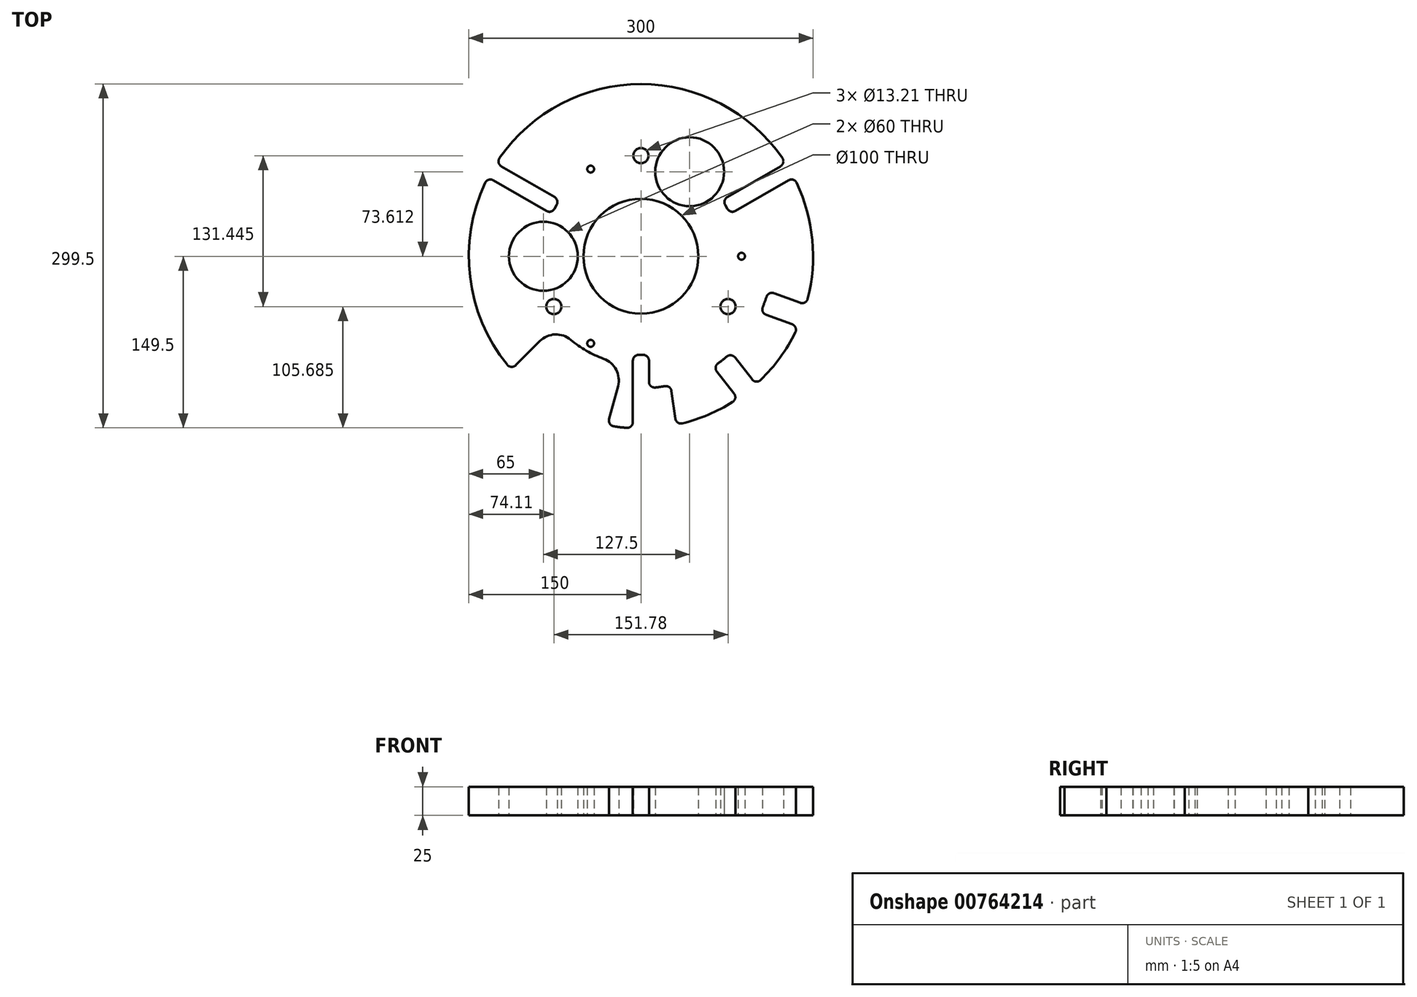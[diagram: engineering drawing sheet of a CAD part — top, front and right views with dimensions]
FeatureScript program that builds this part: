
annotation { "Feature Type Name" : "Feature", "Feature Type Description" : "" }
export const myFeature = defineFeature(function(context is Context, id is Id, definition is map)
    precondition{}
    {
        {
            var Q0;
            Q0=qCreatedBy(makeId("Top.planeOp"),FACE);
            var sketch = newSketch(context, id + "F0", { "sketchPlane" : qUnion([Q0])});
            skLineSegment(sketch, "E0.bottom", {"start": v(-7.02, -85.93) * mm, "end": v(7.03, -85.93) * mm});
            skLineSegment(sketch, "E0.left", {"start": v(-7.02, -85.93) * mm, "end": v(-7.02, -149.84) * mm});
            skLineSegment(sketch, "E0.right", {"start": v(7.03, -85.93) * mm, "end": v(7.03, -114.79) * mm});
            skLineSegment(sketch, "E1", {"start": v(0, 0) * mm, "end": v(20.33, -144.63) * mm, "construction": true});
            skCircle(sketch, "E2", {"center": v(0, 87.63) * mm, "radius": 6.6 * mm});
            skCircle(sketch, "E3.1.0", {"center": v(-75.89, -43.81) * mm, "radius": 6.6 * mm});
            skCircle(sketch, "E3.2.0", {"center": v(75.89, -43.82) * mm, "radius": 6.6 * mm});
            skPoint(sketch, "E3.center", {"position": v(0, 0) * mm});
            skLineSegment(sketch, "E4.1.0", {"start": v(77.93, 36.88) * mm, "end": v(133.27, 68.83) * mm});
            skLineSegment(sketch, "E4.1.1", {"start": v(77.93, 36.88) * mm, "end": v(70.9, 49.05) * mm});
            skLineSegment(sketch, "E4.1.2", {"start": v(70.9, 49.05) * mm, "end": v(126.25, 81) * mm});
            skLineSegment(sketch, "E4.2.0", {"start": v(-70.9, 49.05) * mm, "end": v(-126.25, 81) * mm});
            skLineSegment(sketch, "E4.2.1", {"start": v(-70.9, 49.05) * mm, "end": v(-77.93, 36.88) * mm});
            skLineSegment(sketch, "E4.2.2", {"start": v(-77.93, 36.88) * mm, "end": v(-133.27, 68.83) * mm});
            skArc(sketch, "E5.trimOffspring", {"start": v(-133.27, 68.83) * mm, "mid": v(-148.9, -18.1) * mm, "end": v(-112.9, -98.76) * mm});
            skCircle(sketch, "E6", {"center": v(0, 0) * mm, "radius": 50 * mm});
            skLineSegment(sketch, "E7", {"start": v(0, 0) * mm, "end": v(-98.81, -98.81) * mm, "construction": true});
            skLineSegment(sketch, "E8", {"start": v(0, 0) * mm, "end": v(85.73, -109.22) * mm, "construction": true});
            skLineSegment(sketch, "E9", {"start": v(0, 0) * mm, "end": v(123.83, -45.72) * mm, "construction": true});
            skLineSegment(sketch, "E10.trimOffspring", {"start": v(110.94, -30.3) * mm, "end": v(144.18, -42.57) * mm});
            skLineSegment(sketch, "E11.trimOffspring", {"start": v(104, -49.06) * mm, "end": v(137.25, -61.34) * mm});
            skLineSegment(sketch, "E12.trimOffspring", {"start": v(78.6, -83.94) * mm, "end": v(100.48, -111.82) * mm});
            skLineSegment(sketch, "E13.trimOffspring", {"start": v(62.87, -96.3) * mm, "end": v(84.75, -124.17) * mm});
            skLineSegment(sketch, "E14.trimOffspring", {"start": v(25.85, -112.06) * mm, "end": v(30.73, -146.82) * mm});
            skLineSegment(sketch, "E15.trimOffspring", {"start": v(-98.76, -112.9) * mm, "end": v(-99, -113.14) * mm});
            skLineSegment(sketch, "E16.trimOffspring", {"start": v(-73.87, -59.73) * mm, "end": v(-113.14, -99) * mm});
            skArc(sketch, "E17.trimOffspring", {"start": v(7.03, -114.79) * mm, "mid": v(16.5, -113.81) * mm, "end": v(25.85, -112.06) * mm});
            skArc(sketch, "E18.trimOffspring", {"start": v(62.87, -96.3) * mm, "mid": v(71, -90.46) * mm, "end": v(78.6, -83.94) * mm});
            skArc(sketch, "E19.trimOffspring", {"start": v(104, -49.06) * mm, "mid": v(107.88, -39.83) * mm, "end": v(110.94, -30.3) * mm});
            skArc(sketch, "E20.trimOffspring", {"start": v(30.73, -146.82) * mm, "mid": v(58.77, -138) * mm, "end": v(84.54, -123.9) * mm});
            skPoint(sketch, "E21.start.orphan", {"position": v(7.03, -149.84) * mm});
            skPoint(sketch, "E22.center.orphan", {"position": v(20.33, -144.63) * mm});
            skArc(sketch, "E23.trimOffspring", {"start": v(100.28, -111.56) * mm, "mid": v(121.25, -88.31) * mm, "end": v(136.94, -61.22) * mm});
            skPoint(sketch, "E24.center.orphan", {"position": v(85.73, -109.22) * mm});
            skArc(sketch, "E25.trimOffspring", {"start": v(143.87, -42.46) * mm, "mid": v(149.33, 14.21) * mm, "end": v(133.27, 68.83) * mm});
            skPoint(sketch, "E26.center.orphan", {"position": v(123.83, -45.72) * mm});
            skArc(sketch, "E27.trimOffspring", {"start": v(-29.08, -147.15) * mm, "mid": v(-18.1, -148.9) * mm, "end": v(-7.02, -149.84) * mm});
            skPoint(sketch, "E28.center.orphan", {"position": v(-98.81, -98.81) * mm});
            skArc(sketch, "E29.trimOffspring", {"start": v(126.25, 81) * mm, "mid": v(0, 150) * mm, "end": v(-126.25, 81) * mm});
            skLineSegment(sketch, "E30", {"start": v(0, 0) * mm, "end": v(-43.82, -75.89) * mm, "construction": true});
            skCircle(sketch, "E31", {"center": v(-43.82, -75.89) * mm, "radius": 3 * mm});
            skCircle(sketch, "E32.1.0", {"center": v(87.63, 0) * mm, "radius": 3 * mm});
            skCircle(sketch, "E32.2.0", {"center": v(-43.81, 75.89) * mm, "radius": 3 * mm});
            skLineSegment(sketch, "E33.MirrorCS", {"start": v(-14.8, -93.84) * mm, "end": v(-29.16, -147.48) * mm});
            skArc(sketch, "E34", {"start": v(-73.87, -59.73) * mm, "mid": v(-47.5, -82.27) * mm, "end": v(-14.8, -93.84) * mm});
            skCircle(sketch, "E35", {"center": v(-85, 0) * mm, "radius": 30 * mm});
            skLineSegment(sketch, "E36", {"start": v(-85, 0) * mm, "end": v(0, 0) * mm, "construction": true});
            skLineSegment(sketch, "E37", {"start": v(0, 0) * mm, "end": v(42.5, 73.61) * mm, "construction": true});
            skCircle(sketch, "E38", {"center": v(42.5, 73.61) * mm, "radius": 30 * mm});
            skSolve(sketch);
        }
        {
            var Q0;
            Q0=makeQuery(id+"F0.imprint","IMPRINT",FACE,{"disambiguationData":[TD([[makeQuery(id+"F0.imprint","IMPRINT",EDGE,{"derivedFrom":sQuery(id+"F0.wireOp",EDGE,"E0.bottom")}),1.0]])]});
            extrude(context, id + "F1", {"entities" : qUnion([Q0]), "depth" : 25 * mm, "offsetDistance" : 25 * mm});
        }
        {
            var Q0;
            Q0=makeQuery(id+"F1.opExtrude","SWEPT_EDGE",EDGE,{"disambiguationData":[OSD([sQuery(id+"F0.wireOp",EDGE,"E4.2.1"),sQuery(id+"F0.wireOp",EDGE,"E4.2.2")])]});
            var Q1;
            Q1=makeQuery(id+"F1.opExtrude","SWEPT_EDGE",EDGE,{"disambiguationData":[OSD([sQuery(id+"F0.wireOp",EDGE,"E4.2.0"),sQuery(id+"F0.wireOp",EDGE,"E4.2.1")])]});
            var Q2;
            Q2=makeQuery(id+"F1.opExtrude","SWEPT_EDGE",EDGE,{"disambiguationData":[OSD([sQuery(id+"F0.wireOp",EDGE,"E4.1.1"),sQuery(id+"F0.wireOp",EDGE,"E4.1.2")])]});
            var Q3;
            Q3=makeQuery(id+"F1.opExtrude","SWEPT_EDGE",EDGE,{"disambiguationData":[OSD([sQuery(id+"F0.wireOp",EDGE,"E4.1.0"),sQuery(id+"F0.wireOp",EDGE,"E4.1.1")])]});
            var Q4;
            Q4=makeQuery(id+"F1.opExtrude","SWEPT_EDGE",EDGE,{"disambiguationData":[OSD([sQuery(id+"F0.wireOp",EDGE,"E10.trimOffspring"),sQuery(id+"F0.wireOp",EDGE,"E19.trimOffspring")])]});
            var Q5;
            Q5=makeQuery(id+"F1.opExtrude","SWEPT_EDGE",EDGE,{"disambiguationData":[OSD([sQuery(id+"F0.wireOp",EDGE,"E11.trimOffspring"),sQuery(id+"F0.wireOp",EDGE,"E19.trimOffspring")])]});
            var Q6;
            Q6=makeQuery(id+"F1.opExtrude","SWEPT_EDGE",EDGE,{"disambiguationData":[OSD([sQuery(id+"F0.wireOp",EDGE,"E12.trimOffspring"),sQuery(id+"F0.wireOp",EDGE,"E18.trimOffspring")])]});
            var Q7;
            Q7=makeQuery(id+"F1.opExtrude","SWEPT_EDGE",EDGE,{"disambiguationData":[OSD([sQuery(id+"F0.wireOp",EDGE,"E13.trimOffspring"),sQuery(id+"F0.wireOp",EDGE,"E18.trimOffspring")])]});
            var Q8;
            Q8=makeQuery(id+"F1.opExtrude","SWEPT_EDGE",EDGE,{"disambiguationData":[OSD([sQuery(id+"F0.wireOp",EDGE,"E14.trimOffspring"),sQuery(id+"F0.wireOp",EDGE,"E17.trimOffspring")])]});
            var Q9;
            Q9=makeQuery(id+"F1.opExtrude","SWEPT_EDGE",EDGE,{"disambiguationData":[OSD([sQuery(id+"F0.wireOp",EDGE,"E0.right"),sQuery(id+"F0.wireOp",EDGE,"E17.trimOffspring")])]});
            var Q10;
            Q10=makeQuery(id+"F1.opExtrude","SWEPT_EDGE",EDGE,{"disambiguationData":[OSD([sQuery(id+"F0.wireOp",EDGE,"E0.bottom"),sQuery(id+"F0.wireOp",EDGE,"E0.right")])]});
            var Q11;
            Q11=makeQuery(id+"F1.opExtrude","SWEPT_EDGE",EDGE,{"disambiguationData":[OSD([sQuery(id+"F0.wireOp",EDGE,"E0.bottom"),sQuery(id+"F0.wireOp",EDGE,"E0.left")])]});
            var Q12;
            Q12=makeQuery(id+"F1.opExtrude","SWEPT_EDGE",EDGE,{"disambiguationData":[OSD([sQuery(id+"F0.wireOp",EDGE,"E0.left"),sQuery(id+"F0.wireOp",EDGE,"E27.trimOffspring")])]});
            var Q13;
            Q13=makeQuery(id+"F1.opExtrude","SWEPT_EDGE",EDGE,{"disambiguationData":[OSD([sQuery(id+"F0.wireOp",EDGE,"E27.trimOffspring"),sQuery(id+"F0.wireOp",EDGE,"E33.MirrorCS")])]});
            var Q14;
            Q14=makeQuery(id+"F1.opExtrude","SWEPT_EDGE",EDGE,{"disambiguationData":[OSD([sQuery(id+"F0.wireOp",EDGE,"E5.trimOffspring"),sQuery(id+"F0.wireOp",EDGE,"E16.trimOffspring")])]});
            var Q15;
            Q15=makeQuery(id+"F1.opExtrude","SWEPT_EDGE",EDGE,{"disambiguationData":[OSD([sQuery(id+"F0.wireOp",EDGE,"E14.trimOffspring"),sQuery(id+"F0.wireOp",EDGE,"E20.trimOffspring")])]});
            var Q16;
            Q16=makeQuery(id+"F1.opExtrude","SWEPT_EDGE",EDGE,{"disambiguationData":[OSD([sQuery(id+"F0.wireOp",EDGE,"E13.trimOffspring"),sQuery(id+"F0.wireOp",EDGE,"E20.trimOffspring")])]});
            var Q17;
            Q17=makeQuery(id+"F1.opExtrude","SWEPT_EDGE",EDGE,{"disambiguationData":[OSD([sQuery(id+"F0.wireOp",EDGE,"E12.trimOffspring"),sQuery(id+"F0.wireOp",EDGE,"E23.trimOffspring")])]});
            var Q18;
            Q18=makeQuery(id+"F1.opExtrude","SWEPT_EDGE",EDGE,{"disambiguationData":[OSD([sQuery(id+"F0.wireOp",EDGE,"E11.trimOffspring"),sQuery(id+"F0.wireOp",EDGE,"E23.trimOffspring")])]});
            var Q19;
            Q19=makeQuery(id+"F1.opExtrude","SWEPT_EDGE",EDGE,{"disambiguationData":[OSD([sQuery(id+"F0.wireOp",EDGE,"E10.trimOffspring"),sQuery(id+"F0.wireOp",EDGE,"E25.trimOffspring")])]});
            var Q20;
            Q20=makeQuery(id+"F1.opExtrude","SWEPT_EDGE",EDGE,{"disambiguationData":[OSD([sQuery(id+"F0.wireOp",EDGE,"E4.1.0"),sQuery(id+"F0.wireOp",EDGE,"E25.trimOffspring")])]});
            var Q21;
            Q21=makeQuery(id+"F1.opExtrude","SWEPT_EDGE",EDGE,{"disambiguationData":[OSD([sQuery(id+"F0.wireOp",EDGE,"E4.1.2"),sQuery(id+"F0.wireOp",EDGE,"E29.trimOffspring")])]});
            var Q22;
            Q22=makeQuery(id+"F1.opExtrude","SWEPT_EDGE",EDGE,{"disambiguationData":[OSD([sQuery(id+"F0.wireOp",EDGE,"E4.2.0"),sQuery(id+"F0.wireOp",EDGE,"E29.trimOffspring")])]});
            var Q23;
            Q23=makeQuery(id+"F1.opExtrude","SWEPT_EDGE",EDGE,{"disambiguationData":[OSD([sQuery(id+"F0.wireOp",EDGE,"E4.2.2"),sQuery(id+"F0.wireOp",EDGE,"E5.trimOffspring")])]});
            fillet(context, id + "F2", {"entities" : qUnion([Q0, Q1, Q2, Q3, Q4, Q5, Q6, Q7, Q8, Q9, Q10, Q11, Q12, Q13, Q14, Q15, Q16, Q17, Q18, Q19, Q20, Q21, Q22, Q23]), "radius" : 5 * mm, "tangentPropagation" : true, "allowEdgeOverflow" : false});
        }
        {
            var Q0;
            Q0=makeQuery(id+"F1.opExtrude","SWEPT_EDGE",EDGE,{"disambiguationData":[OSD([sQuery(id+"F0.wireOp",EDGE,"E16.trimOffspring"),sQuery(id+"F0.wireOp",EDGE,"E34")])]});
            var Q1;
            Q1=makeQuery(id+"F1.opExtrude","SWEPT_EDGE",EDGE,{"disambiguationData":[OSD([sQuery(id+"F0.wireOp",EDGE,"E33.MirrorCS"),sQuery(id+"F0.wireOp",EDGE,"E34")])]});
            fillet(context, id + "F3", {"entities" : qUnion([Q0, Q1]), "radius" : 20 * mm, "tangentPropagation" : true, "allowEdgeOverflow" : false});
        }
    });
